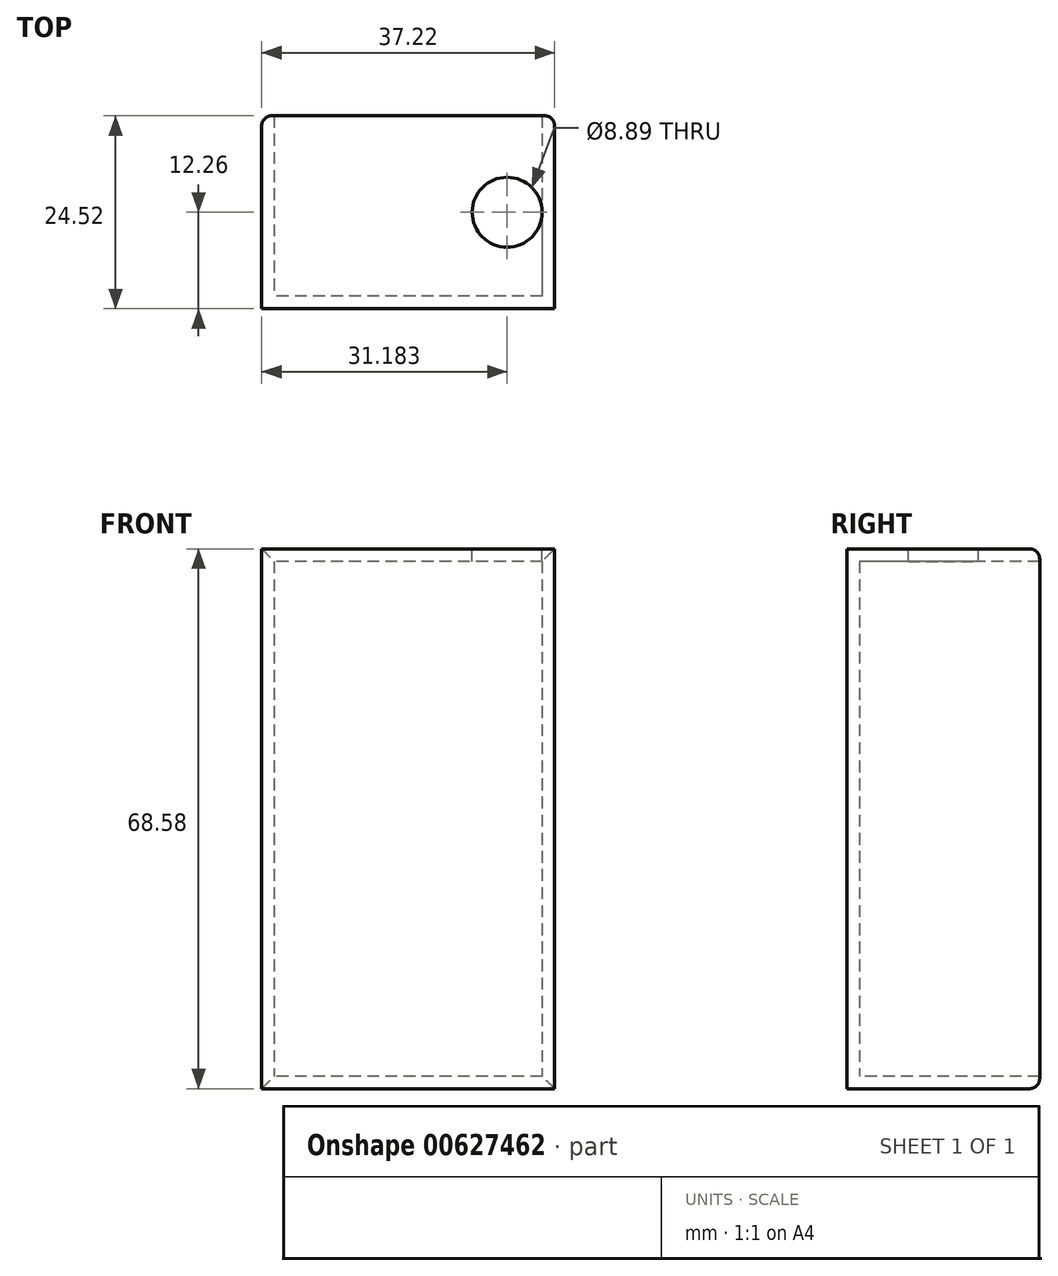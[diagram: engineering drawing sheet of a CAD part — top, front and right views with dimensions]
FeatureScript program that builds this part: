
annotation { "Feature Type Name" : "Feature", "Feature Type Description" : "" }
export const myFeature = defineFeature(function(context is Context, id is Id, definition is map)
    precondition{}
    {
        {
            var Q0;
            Q0=qCreatedBy(makeId("Top.planeOp"),FACE);
            var sketch = newSketch(context, id + "F0", { "sketchPlane" : qUnion([Q0])});
            skLineSegment(sketch, "E0.bottom", {"start": v(18.6, 12.26) * mm, "end": v(-18.6, 12.26) * mm});
            skLineSegment(sketch, "E0.top", {"start": v(18.6, -12.26) * mm, "end": v(-18.6, -12.26) * mm});
            skLineSegment(sketch, "E0.left", {"start": v(18.6, 12.26) * mm, "end": v(18.6, -12.26) * mm});
            skLineSegment(sketch, "E0.right", {"start": v(-18.6, 12.26) * mm, "end": v(-18.6, -12.26) * mm});
            skPoint(sketch, "E0.middle", {"position": v(0, 0) * mm});
            skSolve(sketch);
        }
        {
            var Q0;
            Q0 = qSketchRegion(id + "F0", true);
            extrude(context, id + "F1", {"entities" : qUnion([Q0]), "depth" : 68.58 * mm, "offsetDistance" : 25.4 * mm});
        }
        {
            var Q0;
            Q0=makeQuery(id+"F1.opExtrude","SWEPT_FACE",FACE,{"disambiguationData":[OSD([sQuery(id+"F0.wireOp",EDGE,"E0.bottom")])]});
            shell(context, id + "F2", {"entities" : qUnion([Q0]), "thickness" : 1.59 * mm});
        }
        {
            var Q0;
            Q0=makeQuery(id+"F1.opExtrude","CAP_FACE",FACE,{"disambiguationData":[OSD([sQuery(id+"F0.wireOp",EDGE,"E0.bottom"),sQuery(id+"F0.wireOp",EDGE,"E0.top"),sQuery(id+"F0.wireOp",EDGE,"E0.left"),sQuery(id+"F0.wireOp",EDGE,"E0.right")])],"isStart":false});
            var sketch = newSketch(context, id + "F3", { "sketchPlane" : qUnion([Q0])});
            skCircle(sketch, "E1", {"center": v(12.57, 0) * mm, "radius": 4.45 * mm});
            skSolve(sketch);
        }
        {
            var Q0;
            Q0 = qSketchRegion(id + "F3", true);
            extrude(context, id + "F4", {"entities" : qUnion([Q0]), "operationType" : NewBodyOperationType.REMOVE, "oppositeDirection" : true, "depth" : 1.59 * mm, "offsetDistance" : 25.4 * mm});
        }
        {
            var Q0;
            Q0=makeQuery(id+"F1.opExtrude","SWEPT_EDGE",EDGE,{"disambiguationData":[OSD([sQuery(id+"F0.wireOp",EDGE,"E0.bottom"),sQuery(id+"F0.wireOp",EDGE,"E0.right")])]});
            var Q1;
            Q1=makeQuery(id+"F1.opExtrude","CAP_EDGE",EDGE,{"disambiguationData":[OSD([sQuery(id+"F0.wireOp",EDGE,"E0.bottom")])],"isStart":false});
            var Q2;
            Q2=makeQuery(id+"F1.opExtrude","SWEPT_EDGE",EDGE,{"disambiguationData":[OSD([sQuery(id+"F0.wireOp",EDGE,"E0.bottom"),sQuery(id+"F0.wireOp",EDGE,"E0.left")])]});
            var Q3;
            Q3=makeQuery(id+"F1.opExtrude","CAP_EDGE",EDGE,{"disambiguationData":[OSD([sQuery(id+"F0.wireOp",EDGE,"E0.bottom")])],"isStart":true});
            fillet(context, id + "F5", {"entities" : qUnion([Q0, Q1, Q2, Q3]), "radius" : 1.27 * mm, "tangentPropagation" : true, "allowEdgeOverflow" : false});
        }
    });
